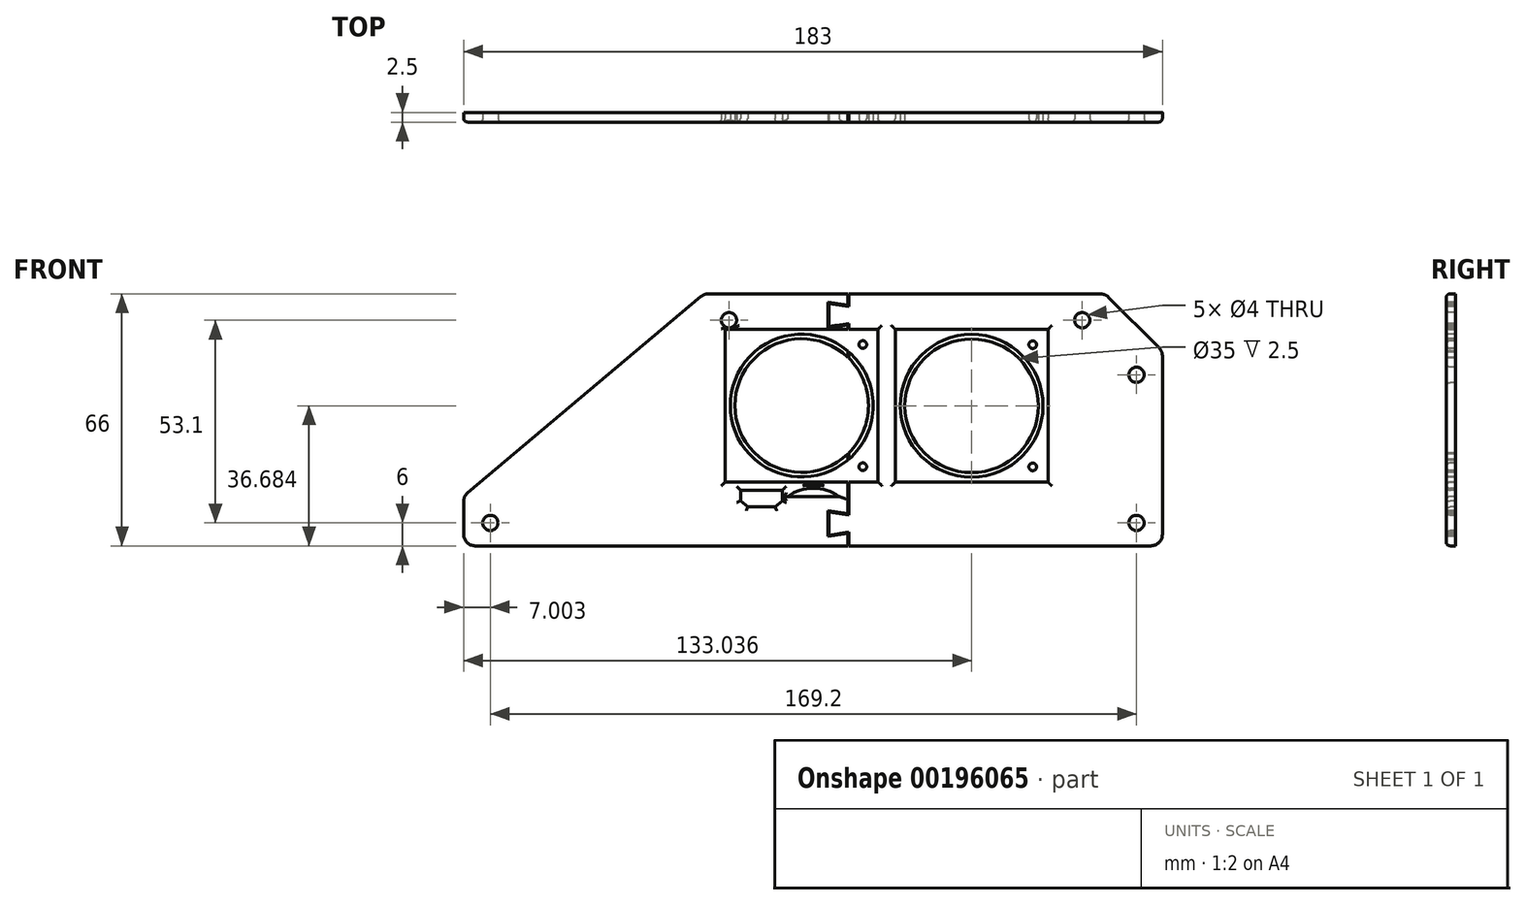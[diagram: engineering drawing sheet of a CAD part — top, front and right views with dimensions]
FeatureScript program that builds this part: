
annotation { "Feature Type Name" : "Feature", "Feature Type Description" : "" }
export const myFeature = defineFeature(function(context is Context, id is Id, definition is map)
    precondition{}
    {
        {
            var Q0;
            Q0=qCreatedBy(makeId("Front.planeOp"),FACE);
            var sketch = newSketch(context, id + "F0", { "sketchPlane" : qUnion([Q0])});
            skLineSegment(sketch, "E0.bottom", {"start": v(89.36, -33) * mm, "end": v(-93.64, -33) * mm});
            skLineSegment(sketch, "E0.top", {"start": v(89.36, 33) * mm, "end": v(-93.64, 33) * mm});
            skLineSegment(sketch, "E0.left", {"start": v(89.36, -33) * mm, "end": v(89.36, 33) * mm});
            skLineSegment(sketch, "E0.right", {"start": v(-93.64, -33) * mm, "end": v(-93.64, 33) * mm});
            skPoint(sketch, "E0.middle", {"position": v(-2.14, 0) * mm});
            skLineSegment(sketch, "E1", {"start": v(89.36, 18) * mm, "end": v(74.36, 33) * mm});
            skLineSegment(sketch, "E2", {"start": v(-93.64, -20) * mm, "end": v(-30.64, 33) * mm});
            skSolve(sketch);
        }
        {
            var Q0;
            {var subQ1=sQuery(id+"F0.wireOp",EDGE,"E0.bottom");Q0=makeQuery(id+"F0.imprint","IMPRINT",FACE,{"disambiguationData":[TD([[makeQuery(id+"F0.imprint","IMPRINT",EDGE,{"derivedFrom":subQ1}),-1.0]])]});}
            extrude(context, id + "F1", {"entities" : qUnion([Q0]), "depth" : 2.5 * mm});
        }
        {
            var Q0;
            Q0=makeQuery(id+"F1.opExtrude","CAP_FACE",FACE,{"disambiguationData":[OSD([sQuery(id+"F0.wireOp",EDGE,"E0.bottom"),sQuery(id+"F0.wireOp",EDGE,"E0.top"),sQuery(id+"F0.wireOp",EDGE,"E0.left"),sQuery(id+"F0.wireOp",EDGE,"E0.right"),sQuery(id+"F0.wireOp",EDGE,"E1"),sQuery(id+"F0.wireOp",EDGE,"E2")])],"isStart":false});
            var sketch = newSketch(context, id + "F2", { "sketchPlane" : qUnion([Q0])});
            skLineSegment(sketch, "E3", {"start": v(-24.14, 26.1) * mm, "end": v(68.36, 26.1) * mm});
            skLineSegment(sketch, "E4", {"start": v(82.56, 11.8) * mm, "end": v(82.56, -27) * mm});
            skLineSegment(sketch, "E5", {"start": v(82.56, -27) * mm, "end": v(-86.64, -27) * mm});
            skCircle(sketch, "E6", {"center": v(-24.14, 26.1) * mm, "radius": 2 * mm});
            skCircle(sketch, "E7", {"center": v(68.36, 26.1) * mm, "radius": 2 * mm});
            skCircle(sketch, "E8", {"center": v(82.56, 11.8) * mm, "radius": 2 * mm});
            skCircle(sketch, "E9", {"center": v(82.56, -27) * mm, "radius": 2 * mm});
            skCircle(sketch, "E10", {"center": v(-86.64, -27) * mm, "radius": 2 * mm});
            skLineSegment(sketch, "E11.bottom", {"start": v(4.66, -22.8) * mm, "end": v(-21.14, -22.8) * mm});
            skLineSegment(sketch, "E11.top", {"start": v(4.66, -17.7) * mm, "end": v(-21.14, -17.7) * mm});
            skLineSegment(sketch, "E11.left", {"start": v(4.66, -22.8) * mm, "end": v(4.66, -17.7) * mm});
            skLineSegment(sketch, "E11.right", {"start": v(-21.14, -22.8) * mm, "end": v(-21.14, -17.7) * mm});
            skPoint(sketch, "E11.middle", {"position": v(-8.24, -20.25) * mm});
            skLineSegment(sketch, "E12.bottom", {"start": v(4.66, -22.8) * mm, "end": v(-8.76, -22.8) * mm});
            skLineSegment(sketch, "E12.top", {"start": v(4.66, -20.08) * mm, "end": v(-8.76, -20.08) * mm});
            skLineSegment(sketch, "E12.left", {"start": v(4.66, -22.8) * mm, "end": v(4.66, -20.08) * mm});
            skLineSegment(sketch, "E12.right", {"start": v(-8.76, -22.8) * mm, "end": v(-8.76, -20.08) * mm});
            skArc(sketch, "E13", {"start": v(4.66, -20.08) * mm, "mid": v(-2.05, -17.94) * mm, "end": v(-8.76, -20.08) * mm});
            skLineSegment(sketch, "E14.bottom", {"start": v(-21.14, -22.8) * mm, "end": v(-10.14, -22.8) * mm});
            skLineSegment(sketch, "E14.top", {"start": v(-21.14, -18.4) * mm, "end": v(-10.14, -18.4) * mm});
            skLineSegment(sketch, "E14.left", {"start": v(-21.14, -22.8) * mm, "end": v(-21.14, -18.4) * mm});
            skLineSegment(sketch, "E14.right", {"start": v(-10.14, -22.8) * mm, "end": v(-10.14, -18.4) * mm});
            skLineSegment(sketch, "E15", {"start": v(-21.14, -21.2) * mm, "end": v(-19.24, -22.8) * mm});
            skLineSegment(sketch, "E16", {"start": v(-10.14, -21.2) * mm, "end": v(-12.04, -22.8) * mm});
            skSolve(sketch);
        }
        {
            var Q0;
            Q0=makeQuery(id+"F2.imprint","IMPRINT",FACE,{"disambiguationData":[TD([[makeQuery(id+"F2.imprint","IMPRINT",EDGE,{"derivedFrom":sQuery(id+"F2.wireOp",EDGE,"E6")}),1.0]])]});
            var Q1;
            Q1=makeQuery(id+"F2.imprint","IMPRINT",FACE,{"disambiguationData":[TD([[makeQuery(id+"F2.imprint","IMPRINT",EDGE,{"derivedFrom":sQuery(id+"F2.wireOp",EDGE,"E7")}),1.0]])]});
            var Q2;
            Q2=makeQuery(id+"F2.imprint","IMPRINT",FACE,{"disambiguationData":[TD([[makeQuery(id+"F2.imprint","IMPRINT",EDGE,{"derivedFrom":sQuery(id+"F2.wireOp",EDGE,"E8")}),1.0]])]});
            var Q3;
            Q3=makeQuery(id+"F2.imprint","IMPRINT",FACE,{"disambiguationData":[TD([[makeQuery(id+"F2.imprint","IMPRINT",EDGE,{"derivedFrom":sQuery(id+"F2.wireOp",EDGE,"E10")}),1.0]])]});
            var Q4;
            {var subQ0=sQuery(id+"F2.wireOp",EDGE,"E5");var subQ1=sQuery(id+"F2.wireOp",EDGE,"E4");var subQ2=makeQuery(id+"F2.imprint","INTERSECT",VERTEX,{"derivedFrom":[subQ1,subQ0]});Q4=makeQuery(id+"F2.imprint","IMPRINT",FACE,{"disambiguationData":[TD([[makeQuery(id+"F2.imprint","IMPRINT",EDGE,{"disambiguationData":[TD([[subQ2,1.0]])],"derivedFrom":subQ1}),-1.0]])]});}
            var Q5;
            {var subQ0=sQuery(id+"F2.wireOp",EDGE,"E5");var subQ1=sQuery(id+"F2.wireOp",EDGE,"E4");var subQ2=makeQuery(id+"F2.imprint","INTERSECT",VERTEX,{"derivedFrom":[subQ1,subQ0]});Q5=makeQuery(id+"F2.imprint","IMPRINT",FACE,{"disambiguationData":[TD([[makeQuery(id+"F2.imprint","IMPRINT",EDGE,{"disambiguationData":[TD([[subQ2,1.0]])],"derivedFrom":subQ1}),1.0]])]});}
            var Q6;
            Q6=makeQuery(id+"F2.imprint","IMPRINT",FACE,{"disambiguationData":[TD([[makeQuery(id+"F2.imprint","IMPRINT",EDGE,{"derivedFrom":sQuery(id+"F2.wireOp",EDGE,"E12.top")}),-1.0]])]});
            var Q7;
            Q7=makeQuery(id+"F2.imprint","IMPRINT",FACE,{"disambiguationData":[TD([[makeQuery(id+"F2.imprint","IMPRINT",EDGE,{"derivedFrom":sQuery(id+"F2.wireOp",EDGE,"E12.bottom")}),-1.0]])]});
            var Q8;
            {var subQ1=sQuery(id+"F2.wireOp",EDGE,"E14.top");Q8=makeQuery(id+"F2.imprint","IMPRINT",FACE,{"disambiguationData":[TD([[makeQuery(id+"F2.imprint","IMPRINT",EDGE,{"derivedFrom":subQ1}),-1.0]])]});}
            extrude(context, id + "F3", {"entities" : qUnion([Q0, Q1, Q2, Q3, Q4, Q5, Q6, Q7, Q8]), "operationType" : NewBodyOperationType.REMOVE, "endBound" : BoundingType.THROUGH_ALL, "oppositeDirection" : true, "depth" : 25 * mm});
        }
        {
            var Q0;
            Q0=makeQuery(id+"F1.opExtrude","CAP_FACE",FACE,{"disambiguationData":[OSD([sQuery(id+"F0.wireOp",EDGE,"E0.bottom"),sQuery(id+"F0.wireOp",EDGE,"E0.top"),sQuery(id+"F0.wireOp",EDGE,"E0.left"),sQuery(id+"F0.wireOp",EDGE,"E0.right"),sQuery(id+"F0.wireOp",EDGE,"E1"),sQuery(id+"F0.wireOp",EDGE,"E2")])],"isStart":false});
            var sketch = newSketch(context, id + "F4", { "sketchPlane" : qUnion([Q0])});
            skCircle(sketch, "E17", {"center": v(-5.1, 3.74) * mm, "radius": 17.5 * mm});
            skCircle(sketch, "E18", {"center": v(-21.1, 19.74) * mm, "radius": 1 * mm});
            skCircle(sketch, "E19.MirrorC", {"center": v(10.9, 19.73) * mm, "radius": 1 * mm});
            skCircle(sketch, "E20.MirrorC", {"center": v(-21.1, -12.27) * mm, "radius": 1 * mm});
            skCircle(sketch, "E21.MirrorC", {"center": v(10.9, -12.27) * mm, "radius": 1 * mm});
            skLineSegment(sketch, "E22.bottom", {"start": v(-25.1, 23.74) * mm, "end": v(14.9, 23.74) * mm});
            skLineSegment(sketch, "E22.top", {"start": v(-25.1, -16.26) * mm, "end": v(14.9, -16.26) * mm});
            skLineSegment(sketch, "E22.left", {"start": v(-25.1, 23.74) * mm, "end": v(-25.1, -16.26) * mm});
            skLineSegment(sketch, "E22.right", {"start": v(14.9, 23.74) * mm, "end": v(14.9, -16.26) * mm});
            skLineSegment(sketch, "E23", {"start": v(-20.77, -4.07) * mm, "end": v(-25.1, -4.07) * mm});
            skLineSegment(sketch, "E24", {"start": v(10.56, -4.07) * mm, "end": v(14.9, -4.07) * mm});
            skLineSegment(sketch, "E25", {"start": v(-20.77, -4.07) * mm, "end": v(10.56, -4.07) * mm});
            skLineSegment(sketch, "E26", {"start": v(-22.1, 7.93) * mm, "end": v(11.88, 7.93) * mm});
            skCircle(sketch, "E27", {"center": v(-5.1, 3.74) * mm, "radius": 18.7 * mm});
            skCircle(sketch, "E28", {"center": v(39.4, 3.68) * mm, "radius": 17.5 * mm});
            skCircle(sketch, "E29", {"center": v(23.4, 19.68) * mm, "radius": 1 * mm});
            skCircle(sketch, "E30.MirrorC", {"center": v(55.4, 19.68) * mm, "radius": 1 * mm});
            skCircle(sketch, "E31.MirrorC", {"center": v(23.4, -12.32) * mm, "radius": 1 * mm});
            skCircle(sketch, "E32.MirrorC", {"center": v(55.4, -12.32) * mm, "radius": 1 * mm});
            skLineSegment(sketch, "E33.bottom", {"start": v(19.4, 23.68) * mm, "end": v(59.4, 23.68) * mm});
            skLineSegment(sketch, "E33.top", {"start": v(19.4, -16.32) * mm, "end": v(59.4, -16.32) * mm});
            skLineSegment(sketch, "E33.left", {"start": v(19.4, 23.68) * mm, "end": v(19.4, -16.32) * mm});
            skLineSegment(sketch, "E33.right", {"start": v(59.4, 23.68) * mm, "end": v(59.4, -16.32) * mm});
            skLineSegment(sketch, "E34", {"start": v(23.73, -4.12) * mm, "end": v(19.4, -4.12) * mm});
            skLineSegment(sketch, "E35", {"start": v(55.06, -4.12) * mm, "end": v(59.4, -4.12) * mm});
            skLineSegment(sketch, "E36", {"start": v(23.73, -4.12) * mm, "end": v(55.06, -4.12) * mm});
            skLineSegment(sketch, "E37", {"start": v(22.4, 7.88) * mm, "end": v(56.39, 7.88) * mm});
            skCircle(sketch, "E38", {"center": v(39.4, 3.68) * mm, "radius": 18.7 * mm});
            skSolve(sketch);
        }
        {
            var Q0;
            Q0=makeQuery(id+"F4.imprint","IMPRINT",FACE,{"disambiguationData":[TD([[makeQuery(id+"F4.imprint","IMPRINT",EDGE,{"derivedFrom":sQuery(id+"F4.wireOp",EDGE,"E18")}),1.0]])]});
            var Q1;
            Q1=makeQuery(id+"F4.imprint","IMPRINT",FACE,{"disambiguationData":[TD([[makeQuery(id+"F4.imprint","IMPRINT",EDGE,{"derivedFrom":sQuery(id+"F4.wireOp",EDGE,"E19.MirrorC")}),-1.0]])]});
            var Q2;
            Q2=makeQuery(id+"F4.imprint","IMPRINT",FACE,{"disambiguationData":[TD([[makeQuery(id+"F4.imprint","IMPRINT",EDGE,{"derivedFrom":sQuery(id+"F4.wireOp",EDGE,"E29")}),1.0]])]});
            var Q3;
            Q3=makeQuery(id+"F4.imprint","IMPRINT",FACE,{"disambiguationData":[TD([[makeQuery(id+"F4.imprint","IMPRINT",EDGE,{"derivedFrom":sQuery(id+"F4.wireOp",EDGE,"E30.MirrorC")}),-1.0]])]});
            var Q4;
            Q4=makeQuery(id+"F4.imprint","IMPRINT",FACE,{"disambiguationData":[TD([[makeQuery(id+"F4.imprint","IMPRINT",EDGE,{"derivedFrom":sQuery(id+"F4.wireOp",EDGE,"E32.MirrorC")}),-1.0]])]});
            var Q5;
            Q5=makeQuery(id+"F4.imprint","IMPRINT",FACE,{"disambiguationData":[TD([[makeQuery(id+"F4.imprint","IMPRINT",EDGE,{"derivedFrom":sQuery(id+"F4.wireOp",EDGE,"E31.MirrorC")}),1.0]])]});
            var Q6;
            Q6=makeQuery(id+"F4.imprint","IMPRINT",FACE,{"disambiguationData":[TD([[makeQuery(id+"F4.imprint","IMPRINT",EDGE,{"derivedFrom":sQuery(id+"F4.wireOp",EDGE,"E21.MirrorC")}),-1.0]])]});
            var Q7;
            Q7=makeQuery(id+"F4.imprint","IMPRINT",FACE,{"disambiguationData":[TD([[makeQuery(id+"F4.imprint","IMPRINT",EDGE,{"derivedFrom":sQuery(id+"F4.wireOp",EDGE,"E20.MirrorC")}),1.0]])]});
            var Q8;
            {var subQ0=sQuery(id+"F4.wireOp",EDGE,"E26");Q8=makeQuery(id+"F4.imprint","IMPRINT",FACE,{"disambiguationData":[TD([[makeQuery(id+"F4.imprint","IMPRINT",EDGE,{"derivedFrom":subQ0}),1.0]])]});}
            var Q9;
            {var subQ0=sQuery(id+"F4.wireOp",EDGE,"E25");Q9=makeQuery(id+"F4.imprint","IMPRINT",FACE,{"disambiguationData":[TD([[makeQuery(id+"F4.imprint","IMPRINT",EDGE,{"derivedFrom":subQ0}),1.0]])]});}
            var Q10;
            {var subQ0=sQuery(id+"F4.wireOp",EDGE,"E25");Q10=makeQuery(id+"F4.imprint","IMPRINT",FACE,{"disambiguationData":[TD([[makeQuery(id+"F4.imprint","IMPRINT",EDGE,{"derivedFrom":subQ0}),-1.0]])]});}
            var Q11;
            {var subQ0=sQuery(id+"F4.wireOp",EDGE,"E37");Q11=makeQuery(id+"F4.imprint","IMPRINT",FACE,{"disambiguationData":[TD([[makeQuery(id+"F4.imprint","IMPRINT",EDGE,{"derivedFrom":subQ0}),1.0]])]});}
            var Q12;
            {var subQ0=sQuery(id+"F4.wireOp",EDGE,"E36");Q12=makeQuery(id+"F4.imprint","IMPRINT",FACE,{"disambiguationData":[TD([[makeQuery(id+"F4.imprint","IMPRINT",EDGE,{"derivedFrom":subQ0}),1.0]])]});}
            var Q13;
            {var subQ0=sQuery(id+"F4.wireOp",EDGE,"E36");Q13=makeQuery(id+"F4.imprint","IMPRINT",FACE,{"disambiguationData":[TD([[makeQuery(id+"F4.imprint","IMPRINT",EDGE,{"derivedFrom":subQ0}),-1.0]])]});}
            extrude(context, id + "F5", {"entities" : qUnion([Q0, Q1, Q2, Q3, Q4, Q5, Q6, Q7, Q8, Q9, Q10, Q11, Q12, Q13]), "operationType" : NewBodyOperationType.REMOVE, "endBound" : BoundingType.THROUGH_ALL, "oppositeDirection" : true, "depth" : 25 * mm});
        }
        {
            var Q0;
            Q0=makeQuery(id+"F1.opExtrude","CAP_FACE",FACE,{"disambiguationData":[OSD([sQuery(id+"F0.wireOp",EDGE,"E0.bottom"),sQuery(id+"F0.wireOp",EDGE,"E0.top"),sQuery(id+"F0.wireOp",EDGE,"E0.left"),sQuery(id+"F0.wireOp",EDGE,"E0.right"),sQuery(id+"F0.wireOp",EDGE,"E1"),sQuery(id+"F0.wireOp",EDGE,"E2")])],"isStart":false});
            var sketch = newSketch(context, id + "F6", { "sketchPlane" : qUnion([Q0])});
            skLineSegment(sketch, "E39", {"start": v(7.22, 33) * mm, "end": v(7.22, -33) * mm});
            skLineSegment(sketch, "E40", {"start": v(6.97, 33) * mm, "end": v(6.97, -33) * mm});
            skLineSegment(sketch, "E41", {"start": v(6.97, 27.44) * mm, "end": v(1.97, 27.44) * mm});
            skLineSegment(sketch, "E42", {"start": v(1.97, 27.44) * mm, "end": v(1.97, 30.46) * mm});
            skLineSegment(sketch, "E43", {"start": v(1.97, 30.46) * mm, "end": v(6.97, 29.7) * mm});
            skLineSegment(sketch, "E44.MirrorCS", {"start": v(1.97, 24.42) * mm, "end": v(6.97, 25.19) * mm});
            skLineSegment(sketch, "E45.MirrorCS", {"start": v(1.97, 27.44) * mm, "end": v(1.97, 24.42) * mm});
            skLineSegment(sketch, "E46", {"start": v(6.97, 30.02) * mm, "end": v(1.72, 30.83) * mm});
            skLineSegment(sketch, "E47", {"start": v(1.72, 30.83) * mm, "end": v(1.72, 27.44) * mm});
            skLineSegment(sketch, "E48.MirrorCS", {"start": v(6.97, 24.86) * mm, "end": v(1.72, 24.06) * mm});
            skLineSegment(sketch, "E49.MirrorCS", {"start": v(1.72, 24.06) * mm, "end": v(1.72, 27.44) * mm});
            skLineSegment(sketch, "E50.MirrorCS", {"start": v(6.97, -27.19) * mm, "end": v(1.97, -27.19) * mm});
            skLineSegment(sketch, "E51.MirrorCS", {"start": v(1.97, -30.21) * mm, "end": v(6.97, -29.44) * mm});
            skLineSegment(sketch, "E52.MirrorCS", {"start": v(6.97, -29.77) * mm, "end": v(1.72, -30.57) * mm});
            skLineSegment(sketch, "E53.MirrorCS", {"start": v(1.97, -27.19) * mm, "end": v(1.97, -30.21) * mm});
            skLineSegment(sketch, "E54.MirrorCS", {"start": v(1.72, -30.57) * mm, "end": v(1.72, -27.19) * mm});
            skLineSegment(sketch, "E55.MirrorCS", {"start": v(1.72, -23.8) * mm, "end": v(1.72, -27.19) * mm});
            skLineSegment(sketch, "E56.MirrorCS", {"start": v(1.97, -27.19) * mm, "end": v(1.97, -24.16) * mm});
            skLineSegment(sketch, "E57.MirrorCS", {"start": v(6.97, -24.6) * mm, "end": v(1.72, -23.8) * mm});
            skLineSegment(sketch, "E58.MirrorCS", {"start": v(1.97, -24.16) * mm, "end": v(6.97, -24.93) * mm});
            skLineSegment(sketch, "E59", {"start": v(6.97, -24.93) * mm, "end": v(7.22, -24.97) * mm});
            skLineSegment(sketch, "E60", {"start": v(6.97, -29.44) * mm, "end": v(7.22, -29.4) * mm});
            skLineSegment(sketch, "E61", {"start": v(6.97, 29.7) * mm, "end": v(7.22, 29.66) * mm});
            skLineSegment(sketch, "E62", {"start": v(6.97, 25.19) * mm, "end": v(7.22, 25.22) * mm});
            skSolve(sketch);
        }
        {
            var Q0;
            Q0=makeQuery(id+"F1.opExtrude","CAP_FACE",FACE,{"disambiguationData":[OSD([sQuery(id+"F0.wireOp",EDGE,"E0.bottom"),sQuery(id+"F0.wireOp",EDGE,"E0.top"),sQuery(id+"F0.wireOp",EDGE,"E0.left"),sQuery(id+"F0.wireOp",EDGE,"E0.right"),sQuery(id+"F0.wireOp",EDGE,"E1"),sQuery(id+"F0.wireOp",EDGE,"E2")])],"isStart":false});
            fillet(context, id + "F7", {"entities" : qUnion([Q0]), "radius" : 1 * mm, "tangentPropagation" : true, "allowEdgeOverflow" : false});
        }
        {
            var Q0;
            Q0=makeQuery(id+"F1.opExtrude","SWEPT_EDGE",EDGE,{"disambiguationData":[OSD([sQuery(id+"F0.wireOp",EDGE,"E0.bottom"),sQuery(id+"F0.wireOp",EDGE,"E0.right")])]});
            var Q1;
            Q1=makeQuery(id+"F1.opExtrude","SWEPT_EDGE",EDGE,{"disambiguationData":[OSD([sQuery(id+"F0.wireOp",EDGE,"E0.right"),sQuery(id+"F0.wireOp",EDGE,"E2")])]});
            var Q2;
            Q2=makeQuery(id+"F1.opExtrude","SWEPT_EDGE",EDGE,{"disambiguationData":[OSD([sQuery(id+"F0.wireOp",EDGE,"E0.top"),sQuery(id+"F0.wireOp",EDGE,"E2")])]});
            var Q3;
            Q3=makeQuery(id+"F1.opExtrude","SWEPT_EDGE",EDGE,{"disambiguationData":[OSD([sQuery(id+"F0.wireOp",EDGE,"E0.top"),sQuery(id+"F0.wireOp",EDGE,"E1")])]});
            var Q4;
            Q4=makeQuery(id+"F1.opExtrude","SWEPT_EDGE",EDGE,{"disambiguationData":[OSD([sQuery(id+"F0.wireOp",EDGE,"E0.left"),sQuery(id+"F0.wireOp",EDGE,"E1")])]});
            var Q5;
            Q5=makeQuery(id+"F1.opExtrude","SWEPT_EDGE",EDGE,{"disambiguationData":[OSD([sQuery(id+"F0.wireOp",EDGE,"E0.bottom"),sQuery(id+"F0.wireOp",EDGE,"E0.left")])]});
            fillet(context, id + "F8", {"entities" : qUnion([Q0, Q1, Q2, Q3, Q4, Q5]), "radius" : 3 * mm, "tangentPropagation" : true, "allowEdgeOverflow" : false});
        }
        {
            var Q0;
            Q0=makeQuery(id+"F6.imprint","IMPRINT",FACE,{"disambiguationData":[TD([[makeQuery(id+"F6.imprint","IMPRINT",EDGE,{"derivedFrom":sQuery(id+"F6.wireOp",EDGE,"E42")}),1.0]])]});
            var Q1;
            Q1=makeQuery(id+"F6.imprint","IMPRINT",FACE,{"disambiguationData":[TD([[makeQuery(id+"F6.imprint","IMPRINT",EDGE,{"derivedFrom":sQuery(id+"F6.wireOp",EDGE,"E53.MirrorCS")}),-1.0]])]});
            var Q2;
            {var subQ0=sQuery(id+"F6.wireOp",EDGE,"E62");Q2=makeQuery(id+"F6.imprint","IMPRINT",FACE,{"disambiguationData":[TD([[makeQuery(id+"F6.imprint","IMPRINT",EDGE,{"derivedFrom":subQ0}),-1.0]])]});}
            var Q3;
            {var subQ3=sQuery(id+"F6.wireOp",EDGE,"E59");Q3=makeQuery(id+"F6.imprint","IMPRINT",FACE,{"disambiguationData":[TD([[makeQuery(id+"F6.imprint","IMPRINT",EDGE,{"derivedFrom":subQ3}),1.0]])]});}
            var Q4;
            {var subQ0=sQuery(id+"F6.wireOp",EDGE,"E39");var subQ1=makeQuery(id+"F5.boolean.opBoolean","COPY",EDGE,{"derivedFrom":makeQuery(id+"F5.opExtrude","CAP_EDGE",EDGE,{"disambiguationData":[OSD([sQuery(id+"F4.wireOp",EDGE,"E28")])],"isStart":true})});var subQ2=makeQuery(id+"F6.imprint","INTERSECT",VERTEX,{"disambiguationData":[OD(0.0)],"derivedFrom":[subQ1,subQ0]});Q4=makeQuery(id+"F6.imprint","IMPRINT",FACE,{"disambiguationData":[TD([[makeQuery(id+"F6.imprint","IMPRINT",EDGE,{"disambiguationData":[TD([[subQ2,-1.0]])],"derivedFrom":subQ0}),-1.0]])]});}
            var Q5;
            {var subQ0=sQuery(id+"F6.wireOp",EDGE,"E61");Q5=makeQuery(id+"F6.imprint","IMPRINT",FACE,{"disambiguationData":[TD([[makeQuery(id+"F6.imprint","IMPRINT",EDGE,{"derivedFrom":subQ0}),1.0]])]});}
            var Q6;
            {var subQ0=sQuery(id+"F6.wireOp",EDGE,"E60");Q6=makeQuery(id+"F6.imprint","IMPRINT",FACE,{"disambiguationData":[TD([[makeQuery(id+"F6.imprint","IMPRINT",EDGE,{"derivedFrom":subQ0}),-1.0]])]});}
            extrude(context, id + "F9", {"entities" : qUnion([Q0, Q1, Q2, Q3, Q4, Q5, Q6]), "operationType" : NewBodyOperationType.REMOVE, "endBound" : BoundingType.THROUGH_ALL, "oppositeDirection" : true, "depth" : 25 * mm});
        }
    });
